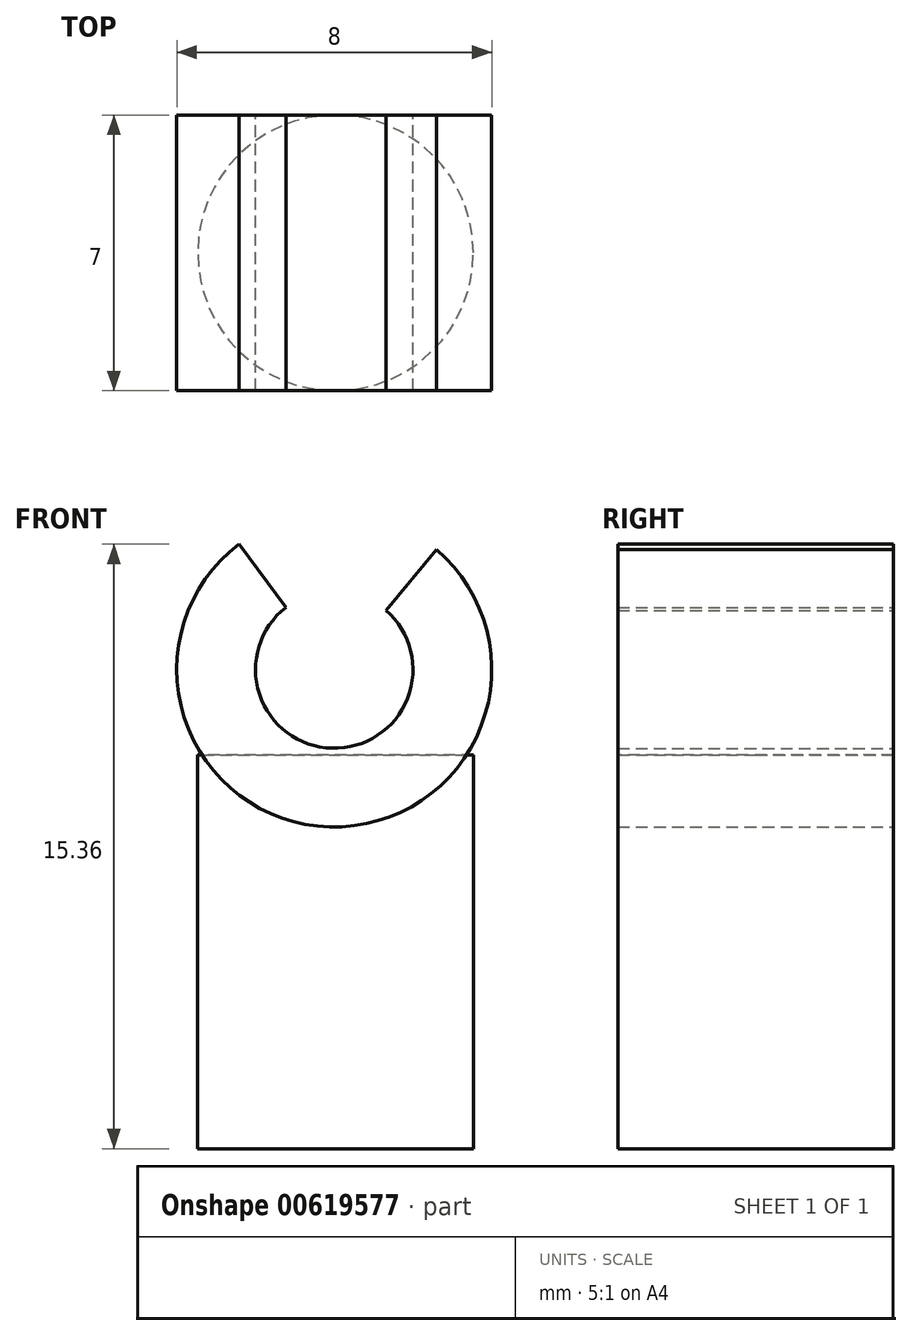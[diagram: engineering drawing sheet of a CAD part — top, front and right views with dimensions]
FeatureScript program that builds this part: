
annotation { "Feature Type Name" : "Feature", "Feature Type Description" : "" }
export const myFeature = defineFeature(function(context is Context, id is Id, definition is map)
    precondition{}
    {
        {
            var Q0;
            Q0=qCreatedBy(makeId("Top.planeOp"),FACE);
            var sketch = newSketch(context, id + "F0", { "sketchPlane" : qUnion([Q0])});
            skLineSegment(sketch, "E0", {"start": v(-33.47, -0.45) * mm, "end": v(47.57, 0.09) * mm, "construction": true});
            skLineSegment(sketch, "E1", {"start": v(0, 46.85) * mm, "end": v(0.63, -49.17) * mm, "construction": true});
            skCircle(sketch, "E2", {"center": v(0, 0) * mm, "radius": 3.5 * mm});
            skSolve(sketch);
        }
        {
            var Q0;
            Q0=makeQuery(id+"F0.imprint","IMPRINT",FACE,{"disambiguationData":[TD([[makeQuery(id+"F0.imprint","IMPRINT",EDGE,{"derivedFrom":sQuery(id+"F0.wireOp",EDGE,"E2")}),1.0]])]});
            extrude(context, id + "F1", {"entities" : qUnion([Q0]), "depth" : 10 * mm, "offsetDistance" : 25 * mm});
        }
        {
            var Q0;
            Q0=qCreatedBy(makeId("Front.planeOp"),FACE);
            var sketch = newSketch(context, id + "F2", { "sketchPlane" : qUnion([Q0])});
            skCircle(sketch, "E3", {"center": v(-0.33, 8.37) * mm, "radius": 2 * mm});
            skCircle(sketch, "E4.0", {"center": v(-0.33, 8.37) * mm, "radius": 4 * mm});
            skLineSegment(sketch, "E5", {"start": v(-0.33, 8.37) * mm, "end": v(-0.22, 12.36) * mm, "construction": true});
            skLineSegment(sketch, "E6", {"start": v(-1.56, 9.95) * mm, "end": v(-2.75, 11.56) * mm});
            skLineSegment(sketch, "E7.MirrorCS", {"start": v(0.98, 9.88) * mm, "end": v(2.26, 11.42) * mm});
            skPoint(sketch, "E8.center.orphan", {"position": v(0, 40.93) * mm});
            skSolve(sketch);
        }
        {
            var Q0;
            {var subQ0=sQuery(id+"F2.wireOp",EDGE,"E6");Q0=makeQuery(id+"F2.imprint","IMPRINT",FACE,{"disambiguationData":[TD([[makeQuery(id+"F2.imprint","IMPRINT",EDGE,{"derivedFrom":subQ0}),1.0]])]});}
            extrude(context, id + "F3", {"entities" : qUnion([Q0]), "depth" : 7 * mm, "offsetDistance" : 25 * mm});
        }
        {
            var Q0;
            Q0=makeQuery(id+"F3.opExtrude","SWEPT_BODY",BODY,{"disambiguationData":[OSD([sQuery(id+"F2.wireOp",EDGE,"E3"),sQuery(id+"F2.wireOp",EDGE,"E4.0"),sQuery(id+"F2.wireOp",EDGE,"E6"),sQuery(id+"F2.wireOp",EDGE,"E7.MirrorCS")])]});
            transform(context, id + "F4", {"entities" : qUnion([Q0]), "transformType" : TransformType.TRANSLATION_3D, "dx" : 0.3 * mm, "dy" : 3.5 * mm, "dz" : 3.8 * mm, "makeCopy" : false});
        }
    });
